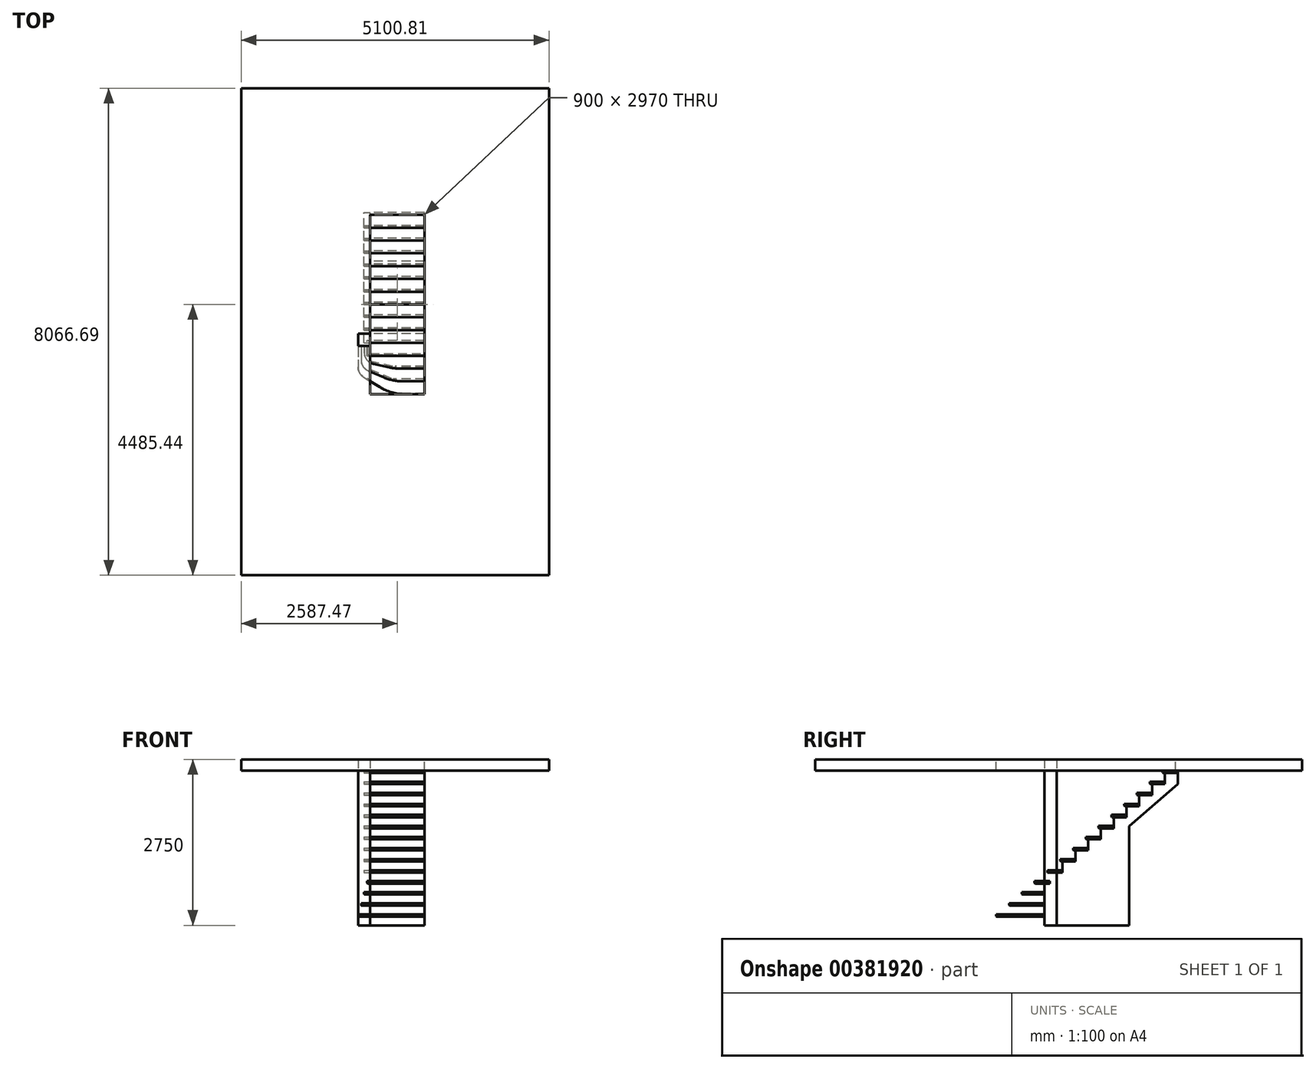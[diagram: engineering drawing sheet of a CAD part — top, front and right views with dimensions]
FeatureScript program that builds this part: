
annotation { "Feature Type Name" : "Feature", "Feature Type Description" : "" }
export const myFeature = defineFeature(function(context is Context, id is Id, definition is map)
    precondition{}
    {
        {
            var Q0;
            Q0=qCreatedBy(makeId("Top.planeOp"),FACE);
            var sketch = newSketch(context, id + "F0", { "sketchPlane" : qUnion([Q0])});
            skLineSegment(sketch, "E0.bottom", {"start": v(0, 2170) * mm, "end": v(-900, 2170) * mm});
            skLineSegment(sketch, "E0.top", {"start": v(0, -800) * mm, "end": v(-900, -800) * mm});
            skLineSegment(sketch, "E0.left", {"start": v(0, 2170) * mm, "end": v(0, -800) * mm});
            skLineSegment(sketch, "E0.right", {"start": v(-900, 2170) * mm, "end": v(-900, -800) * mm});
            skSolve(sketch);
        }
        {
            var Q0;
            Q0=qCreatedBy(makeId("Top.planeOp"),FACE);
            cPlane(context, id + "F1", {"entities" : qUnion([Q0]), "cplaneType" : CPlaneType.OFFSET, "offset" : 2750 * mm, "width" : 150 * mm, "height" : 150 * mm});
        }
        {
            var Q0;
            Q0=qCreatedBy(id+"F1.planeOp",FACE);
            var sketch = newSketch(context, id + "F2", { "sketchPlane" : qUnion([Q0])});
            skLineSegment(sketch, "E1.0", {"start": v(0, 2170) * mm, "end": v(-900, 2170) * mm});
            skLineSegment(sketch, "E1.1", {"start": v(-900, 2170) * mm, "end": v(-900, -800) * mm});
            skLineSegment(sketch, "E1.2", {"start": v(0, -800) * mm, "end": v(-900, -800) * mm});
            skLineSegment(sketch, "E1.3", {"start": v(0, 2170) * mm, "end": v(0, -800) * mm});
            skLineSegment(sketch, "E2.bottom", {"start": v(-3037.47, 4266.25) * mm, "end": v(2063.34, 4266.25) * mm});
            skLineSegment(sketch, "E2.top", {"start": v(-3037.47, -3800.44) * mm, "end": v(2063.34, -3800.44) * mm});
            skLineSegment(sketch, "E2.left", {"start": v(-3037.47, 4266.25) * mm, "end": v(-3037.47, -3800.44) * mm});
            skLineSegment(sketch, "E2.right", {"start": v(2063.34, 4266.25) * mm, "end": v(2063.34, -3800.44) * mm});
            skSolve(sketch);
        }
        {
            var Q0;
            Q0=qCreatedBy(makeId("Top.planeOp"),FACE);
            var sketch = newSketch(context, id + "F3", { "sketchPlane" : qUnion([Q0])});
            skPoint(sketch, "E3.0", {"position": v(0, 0) * mm});
            skLineSegment(sketch, "E4.0", {"start": v(-900, 2170) * mm, "end": v(-900, -800) * mm});
            skLineSegment(sketch, "E5.bottom", {"start": v(-900, 0) * mm, "end": v(-1100, 0) * mm});
            skLineSegment(sketch, "E5.top", {"start": v(-900, 200) * mm, "end": v(-1100, 200) * mm});
            skLineSegment(sketch, "E5.left", {"start": v(-900, 0) * mm, "end": v(-900, 200) * mm});
            skLineSegment(sketch, "E5.right", {"start": v(-1100, 0) * mm, "end": v(-1100, 200) * mm});
            skSolve(sketch);
        }
        {
            var Q0;
            Q0=makeQuery(id+"F3.imprint","IMPRINT",FACE,{"disambiguationData":[TD([[makeQuery(id+"F3.imprint","IMPRINT",EDGE,{"derivedFrom":sQuery(id+"F3.wireOp",EDGE,"E5.bottom")}),-1.0]])]});
            var Q1;
            Q1=qCreatedBy(id+"F1.planeOp",FACE);
            extrude(context, id + "F4", {"entities" : qUnion([Q0]), "endBound" : BoundingType.UP_TO_SURFACE, "endBoundEntityFace" : qUnion([Q1]), "depth" : 25 * mm});
        }
        {
            var Q0;
            Q0=qCreatedBy(makeId("Right.planeOp"),FACE);
            var Q1;
            Q1=sQuery(id+"F0.wireOp",VERTEX,"E0.right.end");
            cPlane(context, id + "F5", {"entities" : qUnion([Q0, Q1]), "cplaneType" : CPlaneType.PLANE_POINT, "offset" : 25 * mm, "width" : 150 * mm, "height" : 150 * mm});
        }
        {
            var Q0;
            Q0=qCreatedBy(id+"F5.planeOp",FACE);
            var sketch = newSketch(context, id + "F6", { "sketchPlane" : qUnion([Q0])});
            skLineSegment(sketch, "E6", {"start": v(-800, 0) * mm, "end": v(-800, 183) * mm});
            skLineSegment(sketch, "E7", {"start": v(-800, 183) * mm, "end": v(-588, 183) * mm});
            skLineSegment(sketch, "E8", {"start": v(-588, 183) * mm, "end": v(-588, 366) * mm});
            skLineSegment(sketch, "E9", {"start": v(-588, 366) * mm, "end": v(-376, 366) * mm});
            skLineSegment(sketch, "E10", {"start": v(-376, 366) * mm, "end": v(-376, 549) * mm});
            skLineSegment(sketch, "E11", {"start": v(-376, 549) * mm, "end": v(-164, 549) * mm});
            skLineSegment(sketch, "E12", {"start": v(-164, 549) * mm, "end": v(-164, 732) * mm});
            skLineSegment(sketch, "E13", {"start": v(-164, 732) * mm, "end": v(48, 732) * mm});
            skLineSegment(sketch, "E14", {"start": v(48, 732) * mm, "end": v(48, 915) * mm});
            skLineSegment(sketch, "E15", {"start": v(48, 915) * mm, "end": v(260, 915) * mm});
            skLineSegment(sketch, "E16", {"start": v(260, 915) * mm, "end": v(260, 1098) * mm});
            skLineSegment(sketch, "E17", {"start": v(260, 1098) * mm, "end": v(472, 1098) * mm});
            skLineSegment(sketch, "E18", {"start": v(472, 1098) * mm, "end": v(472, 1281) * mm});
            skLineSegment(sketch, "E19", {"start": v(472, 1281) * mm, "end": v(684, 1281) * mm});
            skLineSegment(sketch, "E20", {"start": v(684, 1281) * mm, "end": v(684, 1464) * mm});
            skLineSegment(sketch, "E21", {"start": v(684, 1464) * mm, "end": v(896, 1464) * mm});
            skLineSegment(sketch, "E22", {"start": v(896, 1464) * mm, "end": v(896, 1647) * mm});
            skLineSegment(sketch, "E23", {"start": v(896, 1647) * mm, "end": v(1108, 1647) * mm});
            skPoint(sketch, "E24.0", {"position": v(2170, 2750) * mm});
            skLineSegment(sketch, "E25", {"start": v(1108, 1647) * mm, "end": v(1108, 1830) * mm});
            skLineSegment(sketch, "E26", {"start": v(1108, 1830) * mm, "end": v(1320, 1830) * mm});
            skLineSegment(sketch, "E27", {"start": v(1320, 1830) * mm, "end": v(1320, 2013) * mm});
            skLineSegment(sketch, "E28", {"start": v(1320, 2013) * mm, "end": v(1532, 2013) * mm});
            skLineSegment(sketch, "E29", {"start": v(1532, 2013) * mm, "end": v(1532, 2196) * mm});
            skLineSegment(sketch, "E30", {"start": v(1532, 2196) * mm, "end": v(1744, 2196) * mm});
            skLineSegment(sketch, "E31", {"start": v(1744, 2196) * mm, "end": v(1744, 2379) * mm});
            skLineSegment(sketch, "E32", {"start": v(1744, 2379) * mm, "end": v(1956, 2379) * mm});
            skLineSegment(sketch, "E33", {"start": v(1956, 2379) * mm, "end": v(1956, 2562) * mm});
            skLineSegment(sketch, "E34", {"start": v(1956, 2562) * mm, "end": v(2168, 2562) * mm});
            skLineSegment(sketch, "E35", {"start": v(2168, 2562) * mm, "end": v(2168, 2745) * mm});
            skLineSegment(sketch, "E36", {"start": v(2168, 2745) * mm, "end": v(2380, 2745) * mm});
            skSolve(sketch);
        }
        {
            var Q0;
            Q0=qCreatedBy(id+"F5.planeOp",FACE);
            var sketch = newSketch(context, id + "F7", { "sketchPlane" : qUnion([Q0])});
            skLineSegment(sketch, "E37.0", {"start": v(2168, 2745) * mm, "end": v(2380, 2745) * mm});
            skLineSegment(sketch, "E37.1", {"start": v(1956, 2562) * mm, "end": v(2168, 2562) * mm});
            skLineSegment(sketch, "E37.2", {"start": v(1744, 2379) * mm, "end": v(1956, 2379) * mm});
            skLineSegment(sketch, "E37.3", {"start": v(1532, 2196) * mm, "end": v(1744, 2196) * mm});
            skLineSegment(sketch, "E37.4", {"start": v(1320, 2013) * mm, "end": v(1532, 2013) * mm});
            skLineSegment(sketch, "E37.5", {"start": v(1108, 1830) * mm, "end": v(1320, 1830) * mm});
            skLineSegment(sketch, "E37.6", {"start": v(896, 1647) * mm, "end": v(1108, 1647) * mm});
            skLineSegment(sketch, "E37.7", {"start": v(684, 1464) * mm, "end": v(896, 1464) * mm});
            skLineSegment(sketch, "E37.8", {"start": v(472, 1281) * mm, "end": v(684, 1281) * mm});
            skLineSegment(sketch, "E37.9", {"start": v(260, 1098) * mm, "end": v(472, 1098) * mm});
            skLineSegment(sketch, "E37.10", {"start": v(48, 915) * mm, "end": v(260, 915) * mm});
            skLineSegment(sketch, "E38.bottom", {"start": v(1956, 2562) * mm, "end": v(2206, 2562) * mm});
            skLineSegment(sketch, "E38.top", {"start": v(1956, 2522) * mm, "end": v(2206, 2522) * mm});
            skLineSegment(sketch, "E38.left", {"start": v(1956, 2562) * mm, "end": v(1956, 2522) * mm});
            skLineSegment(sketch, "E38.right", {"start": v(2206, 2562) * mm, "end": v(2206, 2522) * mm});
            skLineSegment(sketch, "E39.bottom", {"start": v(1744, 2379) * mm, "end": v(1994, 2379) * mm});
            skLineSegment(sketch, "E39.top", {"start": v(1744, 2339) * mm, "end": v(1994, 2339) * mm});
            skLineSegment(sketch, "E39.left", {"start": v(1744, 2379) * mm, "end": v(1744, 2339) * mm});
            skLineSegment(sketch, "E39.right", {"start": v(1994, 2379) * mm, "end": v(1994, 2339) * mm});
            skLineSegment(sketch, "E40.bottom", {"start": v(1532, 2196) * mm, "end": v(1782, 2196) * mm});
            skLineSegment(sketch, "E40.top", {"start": v(1532, 2156) * mm, "end": v(1782, 2156) * mm});
            skLineSegment(sketch, "E40.left", {"start": v(1532, 2196) * mm, "end": v(1532, 2156) * mm});
            skLineSegment(sketch, "E40.right", {"start": v(1782, 2196) * mm, "end": v(1782, 2156) * mm});
            skLineSegment(sketch, "E41.bottom", {"start": v(1320, 2013) * mm, "end": v(1570, 2013) * mm});
            skLineSegment(sketch, "E41.top", {"start": v(1320, 1973) * mm, "end": v(1570, 1973) * mm});
            skLineSegment(sketch, "E41.left", {"start": v(1320, 2013) * mm, "end": v(1320, 1973) * mm});
            skLineSegment(sketch, "E41.right", {"start": v(1570, 2013) * mm, "end": v(1570, 1973) * mm});
            skLineSegment(sketch, "E42.bottom", {"start": v(1108, 1830) * mm, "end": v(1358, 1830) * mm});
            skLineSegment(sketch, "E42.top", {"start": v(1108, 1790) * mm, "end": v(1358, 1790) * mm});
            skLineSegment(sketch, "E42.left", {"start": v(1108, 1830) * mm, "end": v(1108, 1790) * mm});
            skLineSegment(sketch, "E42.right", {"start": v(1358, 1830) * mm, "end": v(1358, 1790) * mm});
            skLineSegment(sketch, "E43.bottom", {"start": v(896, 1647) * mm, "end": v(1146, 1647) * mm});
            skLineSegment(sketch, "E43.top", {"start": v(896, 1607) * mm, "end": v(1146, 1607) * mm});
            skLineSegment(sketch, "E43.left", {"start": v(896, 1647) * mm, "end": v(896, 1607) * mm});
            skLineSegment(sketch, "E43.right", {"start": v(1146, 1647) * mm, "end": v(1146, 1607) * mm});
            skLineSegment(sketch, "E44.bottom", {"start": v(684, 1464) * mm, "end": v(934, 1464) * mm});
            skLineSegment(sketch, "E44.top", {"start": v(684, 1424) * mm, "end": v(934, 1424) * mm});
            skLineSegment(sketch, "E44.left", {"start": v(684, 1464) * mm, "end": v(684, 1424) * mm});
            skLineSegment(sketch, "E44.right", {"start": v(934, 1464) * mm, "end": v(934, 1424) * mm});
            skLineSegment(sketch, "E45.bottom", {"start": v(472, 1281) * mm, "end": v(722, 1281) * mm});
            skLineSegment(sketch, "E45.top", {"start": v(472, 1241) * mm, "end": v(722, 1241) * mm});
            skLineSegment(sketch, "E45.left", {"start": v(472, 1281) * mm, "end": v(472, 1241) * mm});
            skLineSegment(sketch, "E45.right", {"start": v(722, 1281) * mm, "end": v(722, 1241) * mm});
            skLineSegment(sketch, "E46.bottom", {"start": v(260, 1098) * mm, "end": v(510, 1098) * mm});
            skLineSegment(sketch, "E46.top", {"start": v(260, 1058) * mm, "end": v(510, 1058) * mm});
            skLineSegment(sketch, "E46.left", {"start": v(260, 1098) * mm, "end": v(260, 1058) * mm});
            skLineSegment(sketch, "E46.right", {"start": v(510, 1098) * mm, "end": v(510, 1058) * mm});
            skLineSegment(sketch, "E47.bottom", {"start": v(48, 915) * mm, "end": v(298, 915) * mm});
            skLineSegment(sketch, "E47.top", {"start": v(48, 875) * mm, "end": v(298, 875) * mm});
            skLineSegment(sketch, "E47.left", {"start": v(48, 915) * mm, "end": v(48, 875) * mm});
            skLineSegment(sketch, "E47.right", {"start": v(298, 915) * mm, "end": v(298, 875) * mm});
            skLineSegment(sketch, "E48.0", {"start": v(-164, 732) * mm, "end": v(48, 732) * mm});
            skLineSegment(sketch, "E49.bottom", {"start": v(-164, 732) * mm, "end": v(86, 732) * mm});
            skLineSegment(sketch, "E49.top", {"start": v(-164, 692) * mm, "end": v(86, 692) * mm});
            skLineSegment(sketch, "E49.left", {"start": v(-164, 732) * mm, "end": v(-164, 692) * mm});
            skLineSegment(sketch, "E49.right", {"start": v(86, 732) * mm, "end": v(86, 692) * mm});
            skSolve(sketch);
        }
        {
            var Q0;
            Q0=makeQuery(id+"F7.imprint","IMPRINT",FACE,{"disambiguationData":[TD([[makeQuery(id+"F7.imprint","IMPRINT",EDGE,{"derivedFrom":sQuery(id+"F7.wireOp",EDGE,"E38.top")}),1.0]])]});
            var Q1;
            Q1=makeQuery(id+"F7.imprint","IMPRINT",FACE,{"disambiguationData":[TD([[makeQuery(id+"F7.imprint","IMPRINT",EDGE,{"derivedFrom":sQuery(id+"F7.wireOp",EDGE,"E39.top")}),1.0]])]});
            var Q2;
            Q2=makeQuery(id+"F7.imprint","IMPRINT",FACE,{"disambiguationData":[TD([[makeQuery(id+"F7.imprint","IMPRINT",EDGE,{"derivedFrom":sQuery(id+"F7.wireOp",EDGE,"E40.top")}),1.0]])]});
            var Q3;
            Q3=makeQuery(id+"F7.imprint","IMPRINT",FACE,{"disambiguationData":[TD([[makeQuery(id+"F7.imprint","IMPRINT",EDGE,{"derivedFrom":sQuery(id+"F7.wireOp",EDGE,"E41.top")}),1.0]])]});
            var Q4;
            Q4=makeQuery(id+"F7.imprint","IMPRINT",FACE,{"disambiguationData":[TD([[makeQuery(id+"F7.imprint","IMPRINT",EDGE,{"derivedFrom":sQuery(id+"F7.wireOp",EDGE,"E42.top")}),1.0]])]});
            var Q5;
            Q5=makeQuery(id+"F7.imprint","IMPRINT",FACE,{"disambiguationData":[TD([[makeQuery(id+"F7.imprint","IMPRINT",EDGE,{"derivedFrom":sQuery(id+"F7.wireOp",EDGE,"E43.top")}),1.0]])]});
            var Q6;
            Q6=makeQuery(id+"F7.imprint","IMPRINT",FACE,{"disambiguationData":[TD([[makeQuery(id+"F7.imprint","IMPRINT",EDGE,{"derivedFrom":sQuery(id+"F7.wireOp",EDGE,"E44.top")}),1.0]])]});
            var Q7;
            Q7=makeQuery(id+"F7.imprint","IMPRINT",FACE,{"disambiguationData":[TD([[makeQuery(id+"F7.imprint","IMPRINT",EDGE,{"derivedFrom":sQuery(id+"F7.wireOp",EDGE,"E45.top")}),1.0]])]});
            var Q8;
            Q8=makeQuery(id+"F7.imprint","IMPRINT",FACE,{"disambiguationData":[TD([[makeQuery(id+"F7.imprint","IMPRINT",EDGE,{"derivedFrom":sQuery(id+"F7.wireOp",EDGE,"E46.top")}),1.0]])]});
            var Q9;
            Q9=makeQuery(id+"F7.imprint","IMPRINT",FACE,{"disambiguationData":[TD([[makeQuery(id+"F7.imprint","IMPRINT",EDGE,{"derivedFrom":sQuery(id+"F7.wireOp",EDGE,"E47.top")}),1.0]])]});
            var Q10;
            Q10=makeQuery(id+"F7.imprint","IMPRINT",FACE,{"disambiguationData":[TD([[makeQuery(id+"F7.imprint","IMPRINT",EDGE,{"derivedFrom":sQuery(id+"F7.wireOp",EDGE,"E49.top")}),1.0]])]});
            var Q11;
            Q11=qCreatedBy(makeId("Right.planeOp"),FACE);
            extrude(context, id + "F8", {"entities" : qUnion([Q0, Q1, Q2, Q3, Q4, Q5, Q6, Q7, Q8, Q9, Q10]), "endBound" : BoundingType.UP_TO_SURFACE, "endBoundEntityFace" : qUnion([Q11]), "depth" : 25 * mm});
        }
        {
            var Q0;
            Q0=makeQuery(id+"F8.opExtrude","CAP_FACE",FACE,{"disambiguationData":[OSD([sQuery(id+"F7.wireOp",EDGE,"E38.bottom"),sQuery(id+"F7.wireOp",EDGE,"E38.top"),sQuery(id+"F7.wireOp",EDGE,"E38.left"),sQuery(id+"F7.wireOp",EDGE,"E38.right")])],"isStart":true});
            var Q1;
            Q1=makeQuery(id+"F8.opExtrude","CAP_FACE",FACE,{"disambiguationData":[OSD([sQuery(id+"F7.wireOp",EDGE,"E39.bottom"),sQuery(id+"F7.wireOp",EDGE,"E39.top"),sQuery(id+"F7.wireOp",EDGE,"E39.left"),sQuery(id+"F7.wireOp",EDGE,"E39.right")])],"isStart":true});
            var Q2;
            Q2=makeQuery(id+"F8.opExtrude","CAP_FACE",FACE,{"disambiguationData":[OSD([sQuery(id+"F7.wireOp",EDGE,"E40.bottom"),sQuery(id+"F7.wireOp",EDGE,"E40.top"),sQuery(id+"F7.wireOp",EDGE,"E40.left"),sQuery(id+"F7.wireOp",EDGE,"E40.right")])],"isStart":true});
            var Q3;
            Q3=makeQuery(id+"F8.opExtrude","CAP_FACE",FACE,{"disambiguationData":[OSD([sQuery(id+"F7.wireOp",EDGE,"E41.bottom"),sQuery(id+"F7.wireOp",EDGE,"E41.top"),sQuery(id+"F7.wireOp",EDGE,"E41.left"),sQuery(id+"F7.wireOp",EDGE,"E41.right")])],"isStart":true});
            var Q4;
            Q4=makeQuery(id+"F8.opExtrude","CAP_FACE",FACE,{"disambiguationData":[OSD([sQuery(id+"F7.wireOp",EDGE,"E42.bottom"),sQuery(id+"F7.wireOp",EDGE,"E42.top"),sQuery(id+"F7.wireOp",EDGE,"E42.left"),sQuery(id+"F7.wireOp",EDGE,"E42.right")])],"isStart":true});
            var Q5;
            Q5=makeQuery(id+"F8.opExtrude","CAP_FACE",FACE,{"disambiguationData":[OSD([sQuery(id+"F7.wireOp",EDGE,"E43.bottom"),sQuery(id+"F7.wireOp",EDGE,"E43.top"),sQuery(id+"F7.wireOp",EDGE,"E43.left"),sQuery(id+"F7.wireOp",EDGE,"E43.right")])],"isStart":true});
            var Q6;
            Q6=makeQuery(id+"F8.opExtrude","CAP_FACE",FACE,{"disambiguationData":[OSD([sQuery(id+"F7.wireOp",EDGE,"E44.bottom"),sQuery(id+"F7.wireOp",EDGE,"E44.top"),sQuery(id+"F7.wireOp",EDGE,"E44.left"),sQuery(id+"F7.wireOp",EDGE,"E44.right")])],"isStart":true});
            var Q7;
            Q7=makeQuery(id+"F8.opExtrude","CAP_FACE",FACE,{"disambiguationData":[OSD([sQuery(id+"F7.wireOp",EDGE,"E45.bottom"),sQuery(id+"F7.wireOp",EDGE,"E45.top"),sQuery(id+"F7.wireOp",EDGE,"E45.left"),sQuery(id+"F7.wireOp",EDGE,"E45.right")])],"isStart":true});
            var Q8;
            Q8=makeQuery(id+"F8.opExtrude","CAP_FACE",FACE,{"disambiguationData":[OSD([sQuery(id+"F7.wireOp",EDGE,"E46.bottom"),sQuery(id+"F7.wireOp",EDGE,"E46.top"),sQuery(id+"F7.wireOp",EDGE,"E46.left"),sQuery(id+"F7.wireOp",EDGE,"E46.right")])],"isStart":true});
            var Q9;
            Q9=makeQuery(id+"F8.opExtrude","CAP_FACE",FACE,{"disambiguationData":[OSD([sQuery(id+"F7.wireOp",EDGE,"E47.bottom"),sQuery(id+"F7.wireOp",EDGE,"E47.top"),sQuery(id+"F7.wireOp",EDGE,"E47.left"),sQuery(id+"F7.wireOp",EDGE,"E47.right")])],"isStart":true});
            extrude(context, id + "F9", {"entities" : qUnion([Q0, Q1, Q2, Q3, Q4, Q5, Q6, Q7, Q8, Q9]), "depth" : 100 * mm});
        }
        {
            var Q0;
            Q0=qCreatedBy(id+"F5.planeOp",FACE);
            var sketch = newSketch(context, id + "F10", { "sketchPlane" : qUnion([Q0])});
            skLineSegment(sketch, "E50.0", {"start": v(298, 915) * mm, "end": v(298, 875) * mm});
            skLineSegment(sketch, "E50.1", {"start": v(510, 1098) * mm, "end": v(510, 1058) * mm});
            skLineSegment(sketch, "E50.2", {"start": v(722, 1281) * mm, "end": v(722, 1241) * mm});
            skLineSegment(sketch, "E50.3", {"start": v(934, 1464) * mm, "end": v(934, 1424) * mm});
            skLineSegment(sketch, "E50.4", {"start": v(1146, 1647) * mm, "end": v(1146, 1607) * mm});
            skLineSegment(sketch, "E50.5", {"start": v(1358, 1830) * mm, "end": v(1358, 1790) * mm});
            skLineSegment(sketch, "E50.6", {"start": v(1570, 2013) * mm, "end": v(1570, 1973) * mm});
            skLineSegment(sketch, "E50.7", {"start": v(1782, 2196) * mm, "end": v(1782, 2156) * mm});
            skLineSegment(sketch, "E50.8", {"start": v(1994, 2379) * mm, "end": v(1994, 2339) * mm});
            skLineSegment(sketch, "E50.9", {"start": v(2206, 2562) * mm, "end": v(2206, 2522) * mm});
            skLineSegment(sketch, "E51", {"start": v(298, 915) * mm, "end": v(298, 1058) * mm});
            skLineSegment(sketch, "E52", {"start": v(298, 1058) * mm, "end": v(510, 1058) * mm});
            skLineSegment(sketch, "E53", {"start": v(510, 1098) * mm, "end": v(510, 1241) * mm});
            skLineSegment(sketch, "E54", {"start": v(510, 1241) * mm, "end": v(722, 1241) * mm});
            skLineSegment(sketch, "E55", {"start": v(722, 1281) * mm, "end": v(722, 1424) * mm});
            skLineSegment(sketch, "E56", {"start": v(722, 1424) * mm, "end": v(934, 1424) * mm});
            skLineSegment(sketch, "E57", {"start": v(934, 1464) * mm, "end": v(934, 1607) * mm});
            skLineSegment(sketch, "E58", {"start": v(934, 1607) * mm, "end": v(1146, 1607) * mm});
            skLineSegment(sketch, "E59", {"start": v(1146, 1647) * mm, "end": v(1146, 1790) * mm});
            skLineSegment(sketch, "E60", {"start": v(1146, 1790) * mm, "end": v(1358, 1790) * mm});
            skLineSegment(sketch, "E61", {"start": v(1358, 1830) * mm, "end": v(1358, 1973) * mm});
            skLineSegment(sketch, "E62", {"start": v(1358, 1973) * mm, "end": v(1570, 1973) * mm});
            skLineSegment(sketch, "E63", {"start": v(1570, 2013) * mm, "end": v(1570, 2156) * mm});
            skLineSegment(sketch, "E64", {"start": v(1570, 2156) * mm, "end": v(1782, 2156) * mm});
            skLineSegment(sketch, "E65", {"start": v(1782, 2196) * mm, "end": v(1782, 2339) * mm});
            skLineSegment(sketch, "E66", {"start": v(1782, 2339) * mm, "end": v(1994, 2339) * mm});
            skLineSegment(sketch, "E67", {"start": v(1994, 2379) * mm, "end": v(1994, 2522) * mm});
            skLineSegment(sketch, "E68", {"start": v(1994, 2522) * mm, "end": v(2206, 2522) * mm});
            skPoint(sketch, "E69.0", {"position": v(200, 875) * mm});
            skLineSegment(sketch, "E70", {"start": v(298, 875) * mm, "end": v(200, 875) * mm});
            skLineSegment(sketch, "E71", {"start": v(200, 0) * mm, "end": v(1400, 0) * mm});
            skLineSegment(sketch, "E72", {"start": v(1400, 0) * mm, "end": v(1400, 1973) * mm});
            skLineSegment(sketch, "E73", {"start": v(200, 875) * mm, "end": v(200, 0) * mm});
            skLineSegment(sketch, "E74", {"start": v(2206, 2522) * mm, "end": v(2206, 2339) * mm});
            skLineSegment(sketch, "E75", {"start": v(1146, 1607) * mm, "end": v(1146, 1424) * mm});
            skLineSegment(sketch, "E76", {"start": v(1146, 1424) * mm, "end": v(2206, 2339) * mm});
            skSolve(sketch);
        }
        {
            var Q0;
            Q0=makeQuery(id+"F10.imprint","IMPRINT",FACE,{"disambiguationData":[TD([[makeQuery(id+"F10.imprint","IMPRINT",EDGE,{"derivedFrom":sQuery(id+"F10.wireOp",EDGE,"E50.0")}),1.0]])]});
            var Q1;
            Q1=makeQuery(id+"F10.imprint","IMPRINT",FACE,{"disambiguationData":[TD([[makeQuery(id+"F10.imprint","IMPRINT",EDGE,{"derivedFrom":sQuery(id+"F10.wireOp",EDGE,"E50.4")}),1.0]])]});
            var Q2;
            {var subQ0=sQuery(id+"F10.wireOp",EDGE,"E50.6");Q2=makeQuery(id+"F10.imprint","IMPRINT",FACE,{"disambiguationData":[TD([[makeQuery(id+"F10.imprint","IMPRINT",EDGE,{"derivedFrom":subQ0}),1.0]])]});}
            var Q3;
            Q3=qCreatedBy(makeId("Right.planeOp"),FACE);
            extrude(context, id + "F11", {"entities" : qUnion([Q0, Q1, Q2]), "endBound" : BoundingType.UP_TO_SURFACE, "endBoundEntityFace" : qUnion([Q3]), "depth" : 25 * mm});
        }
        {
            var Q0;
            Q0=makeQuery(id+"F8.opExtrude","CAP_FACE",FACE,{"disambiguationData":[OSD([sQuery(id+"F7.wireOp",EDGE,"E49.bottom"),sQuery(id+"F7.wireOp",EDGE,"E49.top"),sQuery(id+"F7.wireOp",EDGE,"E49.left"),sQuery(id+"F7.wireOp",EDGE,"E49.right")])],"isStart":true});
            extrude(context, id + "F12", {"entities" : qUnion([Q0]), "depth" : 50 * mm});
        }
        {
            var Q0;
            Q0=qCreatedBy(makeId("Top.planeOp"),FACE);
            var Q1;
            Q1=sQuery(id+"F6.wireOp",VERTEX,"E11.start");
            cPlane(context, id + "F13", {"entities" : qUnion([Q0, Q1]), "cplaneType" : CPlaneType.PLANE_POINT, "offset" : 25 * mm, "width" : 150 * mm, "height" : 150 * mm});
        }
        {
            var Q0;
            Q0=qCreatedBy(makeId("Top.planeOp"),FACE);
            var Q1;
            Q1=sQuery(id+"F6.wireOp",VERTEX,"E9.start");
            cPlane(context, id + "F14", {"entities" : qUnion([Q0, Q1]), "cplaneType" : CPlaneType.PLANE_POINT, "offset" : 25 * mm, "width" : 150 * mm, "height" : 150 * mm});
        }
        {
            var Q0;
            Q0=qCreatedBy(makeId("Top.planeOp"),FACE);
            var Q1;
            Q1=sQuery(id+"F6.wireOp",VERTEX,"E7.start");
            cPlane(context, id + "F15", {"entities" : qUnion([Q0, Q1]), "cplaneType" : CPlaneType.PLANE_POINT, "offset" : 25 * mm, "width" : 150 * mm, "height" : 150 * mm});
        }
        {
            var Q0;
            Q0=qCreatedBy(id+"F13.planeOp",FACE);
            var sketch = newSketch(context, id + "F16", { "sketchPlane" : qUnion([Q0])});
            skPoint(sketch, "E77.0", {"position": v(-900, -376) * mm});
            skLineSegment(sketch, "E78.bottom", {"start": v(-500, -376) * mm, "end": v(0, -376) * mm});
            skLineSegment(sketch, "E78.top", {"start": v(-900, -126) * mm, "end": v(0, -126) * mm});
            skLineSegment(sketch, "E78.right", {"start": v(0, -376) * mm, "end": v(0, -126) * mm});
            skLineSegment(sketch, "E79", {"start": v(-1000, -126) * mm, "end": v(-1000, -266) * mm});
            skLineSegment(sketch, "E80", {"start": v(-1000, -266) * mm, "end": v(-500, -376) * mm});
            skLineSegment(sketch, "E81.0", {"start": v(-900, 0) * mm, "end": v(-1000, 0) * mm});
            skLineSegment(sketch, "E82", {"start": v(-900, -126) * mm, "end": v(-900, 0) * mm});
            skLineSegment(sketch, "E83", {"start": v(-1000, -126) * mm, "end": v(-1000, 0) * mm});
            skPoint(sketch, "E84.orphan", {"position": v(-1100, 0) * mm});
            skSolve(sketch);
        }
        {
            var Q0;
            Q0=makeQuery(id+"F16.imprint","IMPRINT",FACE,{"disambiguationData":[TD([[makeQuery(id+"F16.imprint","IMPRINT",EDGE,{"derivedFrom":sQuery(id+"F16.wireOp",EDGE,"E78.bottom")}),1.0]])]});
            extrude(context, id + "F17", {"entities" : qUnion([Q0]), "oppositeDirection" : true, "depth" : 40 * mm});
        }
        {
            var Q0;
            Q0=qCreatedBy(id+"F14.planeOp",FACE);
            var sketch = newSketch(context, id + "F18", { "sketchPlane" : qUnion([Q0])});
            skPoint(sketch, "E85.0", {"position": v(-900, -588) * mm});
            skLineSegment(sketch, "E86", {"start": v(-525, -588) * mm, "end": v(0, -588) * mm});
            skLineSegment(sketch, "E87", {"start": v(0, -588) * mm, "end": v(0, -338) * mm});
            skPoint(sketch, "E88", {"position": v(-525, -588) * mm});
            skPoint(sketch, "E89", {"position": v(-1000, -226) * mm});
            skLineSegment(sketch, "E90", {"start": v(0, -338) * mm, "end": v(-490.9, -338) * mm});
            skLineSegment(sketch, "E91", {"start": v(-900, -248) * mm, "end": v(-490.9, -338) * mm});
            skPoint(sketch, "E92.orphan", {"position": v(-1000, -266) * mm});
            skLineSegment(sketch, "E93", {"start": v(-1050, -226) * mm, "end": v(-1050, -366) * mm});
            skLineSegment(sketch, "E94", {"start": v(-1050, -366) * mm, "end": v(-525, -588) * mm});
            skLineSegment(sketch, "E95.0", {"start": v(-900, 0) * mm, "end": v(-1050, 0) * mm});
            skLineSegment(sketch, "E96", {"start": v(-900, 0) * mm, "end": v(-900, -248) * mm});
            skLineSegment(sketch, "E97", {"start": v(-1050, -226) * mm, "end": v(-1050, 0) * mm});
            skPoint(sketch, "E98.orphan", {"position": v(-1100, 0) * mm});
            skSolve(sketch);
        }
        {
            var Q0;
            Q0=makeQuery(id+"F18.imprint","IMPRINT",FACE,{"disambiguationData":[TD([[makeQuery(id+"F18.imprint","IMPRINT",EDGE,{"derivedFrom":sQuery(id+"F18.wireOp",EDGE,"E86")}),1.0]])]});
            extrude(context, id + "F19", {"entities" : qUnion([Q0]), "oppositeDirection" : true, "depth" : 40 * mm});
        }
        {
            var Q0;
            Q0=qCreatedBy(id+"F15.planeOp",FACE);
            var sketch = newSketch(context, id + "F20", { "sketchPlane" : qUnion([Q0])});
            skPoint(sketch, "E99.0", {"position": v(-900, -800) * mm});
            skLineSegment(sketch, "E100", {"start": v(-550, -800) * mm, "end": v(0, -800) * mm});
            skLineSegment(sketch, "E101", {"start": v(0, -800) * mm, "end": v(0, -550) * mm});
            skLineSegment(sketch, "E102", {"start": v(0, -550) * mm, "end": v(-520.27, -550) * mm});
            skPoint(sketch, "E103", {"position": v(-550, -800) * mm});
            skPoint(sketch, "E104", {"position": v(-1050, -326) * mm});
            skLineSegment(sketch, "E105", {"start": v(-900, -389.43) * mm, "end": v(-520.27, -550) * mm});
            skLineSegment(sketch, "E106.0", {"start": v(-900, 0) * mm, "end": v(-1100, 0) * mm});
            skLineSegment(sketch, "E107", {"start": v(-900, 0) * mm, "end": v(-900, -389.43) * mm});
            skLineSegment(sketch, "E108", {"start": v(-900, -389.43) * mm, "end": v(-900, 0) * mm});
            skLineSegment(sketch, "E109", {"start": v(-1100, -326) * mm, "end": v(-1100, -466) * mm});
            skPoint(sketch, "E110.orphan", {"position": v(-1050, -366) * mm});
            skPoint(sketch, "E111.0.end.orphan", {"position": v(-1050, 0) * mm});
            skLineSegment(sketch, "E112", {"start": v(-1100, 0) * mm, "end": v(-1100, -326) * mm});
            skLineSegment(sketch, "E113", {"start": v(-1100, -466) * mm, "end": v(-550, -800) * mm});
            skSolve(sketch);
        }
        {
            var Q0;
            Q0=makeQuery(id+"F20.imprint","IMPRINT",FACE,{"disambiguationData":[TD([[makeQuery(id+"F20.imprint","IMPRINT",EDGE,{"derivedFrom":sQuery(id+"F20.wireOp",EDGE,"E100")}),1.0]])]});
            extrude(context, id + "F21", {"entities" : qUnion([Q0]), "oppositeDirection" : true, "depth" : 40 * mm});
        }
        {
            var Q0;
            Q0=makeQuery(id+"F21.opExtrude","CAP_FACE",FACE,{"disambiguationData":[OSD([sQuery(id+"F20.wireOp",EDGE,"E100"),sQuery(id+"F20.wireOp",EDGE,"E101"),sQuery(id+"F20.wireOp",EDGE,"E102"),sQuery(id+"F20.wireOp",EDGE,"E105"),sQuery(id+"F20.wireOp",EDGE,"E106.0"),sQuery(id+"F20.wireOp",EDGE,"E108"),sQuery(id+"F20.wireOp",EDGE,"E109"),sQuery(id+"F20.wireOp",EDGE,"E112"),sQuery(id+"F20.wireOp",EDGE,"E113")])],"isStart":false});
            var sketch = newSketch(context, id + "F22", { "sketchPlane" : qUnion([Q0])});
            skLineSegment(sketch, "E114.0", {"start": v(-538.8, 760) * mm, "end": v(0, 760) * mm});
            skLineSegment(sketch, "E114.1", {"start": v(-1060, 443.5) * mm, "end": v(-538.8, 760) * mm});
            skLineSegment(sketch, "E114.2", {"start": v(-1060, 0) * mm, "end": v(-1060, 443.5) * mm});
            skSolve(sketch);
        }
        {
            var Q0;
            Q0=sQuery(id+"F22.wireOp",EDGE,"E114.2");
            var Q1;
            Q1=sQuery(id+"F22.wireOp",EDGE,"E114.1");
            var Q2;
            Q2=sQuery(id+"F22.wireOp",EDGE,"E114.0");
            var Q3;
            Q3=makeQuery(id+"F4.opExtrude","CAP_FACE",FACE,{"disambiguationData":[OSD([sQuery(id+"F3.wireOp",EDGE,"E5.bottom"),sQuery(id+"F3.wireOp",EDGE,"E5.top"),sQuery(id+"F3.wireOp",EDGE,"E5.left"),sQuery(id+"F3.wireOp",EDGE,"E5.right")])],"isStart":true});
            extrude(context, id + "F23", {"bodyType" : ToolBodyType.SURFACE, "surfaceEntities" : qUnion([Q0, Q1, Q2]), "endBound" : BoundingType.UP_TO_SURFACE, "endBoundEntityFace" : qUnion([Q3]), "depth" : 25 * mm});
        }
        {
            var Q0;
            Q0=makeQuery(id+"F19.opExtrude","CAP_FACE",FACE,{"disambiguationData":[OSD([sQuery(id+"F18.wireOp",EDGE,"E86"),sQuery(id+"F18.wireOp",EDGE,"E87"),sQuery(id+"F18.wireOp",EDGE,"E90"),sQuery(id+"F18.wireOp",EDGE,"E91"),sQuery(id+"F18.wireOp",EDGE,"E93"),sQuery(id+"F18.wireOp",EDGE,"E94"),sQuery(id+"F18.wireOp",EDGE,"E95.0"),sQuery(id+"F18.wireOp",EDGE,"E96"),sQuery(id+"F18.wireOp",EDGE,"E97")])],"isStart":false});
            var sketch = newSketch(context, id + "F24", { "sketchPlane" : qUnion([Q0])});
            skLineSegment(sketch, "E115.0", {"start": v(-1010, 339.49) * mm, "end": v(-1010, 0) * mm});
            skLineSegment(sketch, "E115.1", {"start": v(-1010, 339.49) * mm, "end": v(-516.9, 548) * mm});
            skLineSegment(sketch, "E115.2", {"start": v(-516.9, 548) * mm, "end": v(0, 548) * mm});
            skSolve(sketch);
        }
        {
            var Q0;
            Q0=sQuery(id+"F24.wireOp",EDGE,"E115.0");
            var Q1;
            Q1=sQuery(id+"F24.wireOp",EDGE,"E115.1");
            var Q2;
            Q2=sQuery(id+"F24.wireOp",EDGE,"E115.2");
            var Q3;
            Q3=makeQuery(id+"F21.opExtrude","CAP_FACE",FACE,{"disambiguationData":[OSD([sQuery(id+"F20.wireOp",EDGE,"E100"),sQuery(id+"F20.wireOp",EDGE,"E101"),sQuery(id+"F20.wireOp",EDGE,"E102"),sQuery(id+"F20.wireOp",EDGE,"E105"),sQuery(id+"F20.wireOp",EDGE,"E106.0"),sQuery(id+"F20.wireOp",EDGE,"E108"),sQuery(id+"F20.wireOp",EDGE,"E109"),sQuery(id+"F20.wireOp",EDGE,"E112"),sQuery(id+"F20.wireOp",EDGE,"E113")])],"isStart":true});
            extrude(context, id + "F25", {"bodyType" : ToolBodyType.SURFACE, "surfaceEntities" : qUnion([Q0, Q1, Q2]), "endBound" : BoundingType.UP_TO_SURFACE, "endBoundEntityFace" : qUnion([Q3]), "depth" : 25 * mm});
        }
        {
            var Q0;
            Q0=makeQuery(id+"F17.opExtrude","CAP_FACE",FACE,{"disambiguationData":[OSD([sQuery(id+"F16.wireOp",EDGE,"E78.bottom"),sQuery(id+"F16.wireOp",EDGE,"E78.top"),sQuery(id+"F16.wireOp",EDGE,"E78.right"),sQuery(id+"F16.wireOp",EDGE,"E79"),sQuery(id+"F16.wireOp",EDGE,"E80"),sQuery(id+"F16.wireOp",EDGE,"E81.0"),sQuery(id+"F16.wireOp",EDGE,"E82"),sQuery(id+"F16.wireOp",EDGE,"E83")])],"isStart":false});
            var sketch = newSketch(context, id + "F26", { "sketchPlane" : qUnion([Q0])});
            skLineSegment(sketch, "E116.0", {"start": v(-960, 233.84) * mm, "end": v(-960, 0) * mm});
            skLineSegment(sketch, "E116.1", {"start": v(-960, 233.84) * mm, "end": v(-495.65, 336) * mm});
            skLineSegment(sketch, "E116.2", {"start": v(-495.65, 336) * mm, "end": v(0, 336) * mm});
            skSolve(sketch);
        }
        {
            var Q0;
            Q0=sQuery(id+"F26.wireOp",EDGE,"E116.0");
            var Q1;
            Q1=sQuery(id+"F26.wireOp",EDGE,"E116.1");
            var Q2;
            Q2=sQuery(id+"F26.wireOp",EDGE,"E116.2");
            var Q3;
            Q3=makeQuery(id+"F19.opExtrude","CAP_FACE",FACE,{"disambiguationData":[OSD([sQuery(id+"F18.wireOp",EDGE,"E86"),sQuery(id+"F18.wireOp",EDGE,"E87"),sQuery(id+"F18.wireOp",EDGE,"E90"),sQuery(id+"F18.wireOp",EDGE,"E91"),sQuery(id+"F18.wireOp",EDGE,"E93"),sQuery(id+"F18.wireOp",EDGE,"E94"),sQuery(id+"F18.wireOp",EDGE,"E95.0"),sQuery(id+"F18.wireOp",EDGE,"E96"),sQuery(id+"F18.wireOp",EDGE,"E97")])],"isStart":true});
            extrude(context, id + "F27", {"bodyType" : ToolBodyType.SURFACE, "surfaceEntities" : qUnion([Q0, Q1, Q2]), "endBound" : BoundingType.UP_TO_SURFACE, "endBoundEntityFace" : qUnion([Q3]), "depth" : 25 * mm});
        }
        {
            var Q0;
            Q0=makeQuery(id+"F8.opExtrude","SWEPT_FACE",FACE,{"disambiguationData":[OSD([sQuery(id+"F7.wireOp",EDGE,"E49.top")])]});
            var sketch = newSketch(context, id + "F28", { "sketchPlane" : qUnion([Q0])});
            skLineSegment(sketch, "E117.0", {"start": v(-910, 124) * mm, "end": v(-910, -86) * mm});
            skLineSegment(sketch, "E117.1", {"start": v(-910, 124) * mm, "end": v(-900, 124) * mm});
            skLineSegment(sketch, "E117.2", {"start": v(0, 124) * mm, "end": v(-900, 124) * mm});
            skSolve(sketch);
        }
        {
            var Q0;
            Q0=sQuery(id+"F28.wireOp",EDGE,"E117.0");
            var Q1;
            Q1=sQuery(id+"F28.wireOp",EDGE,"E117.1");
            var Q2;
            Q2=sQuery(id+"F28.wireOp",EDGE,"E117.2");
            var Q3;
            Q3=makeQuery(id+"F17.opExtrude","CAP_FACE",FACE,{"disambiguationData":[OSD([sQuery(id+"F16.wireOp",EDGE,"E78.bottom"),sQuery(id+"F16.wireOp",EDGE,"E78.top"),sQuery(id+"F16.wireOp",EDGE,"E78.right"),sQuery(id+"F16.wireOp",EDGE,"E79"),sQuery(id+"F16.wireOp",EDGE,"E80"),sQuery(id+"F16.wireOp",EDGE,"E81.0"),sQuery(id+"F16.wireOp",EDGE,"E82"),sQuery(id+"F16.wireOp",EDGE,"E83")])],"isStart":true});
            extrude(context, id + "F29", {"bodyType" : ToolBodyType.SURFACE, "surfaceEntities" : qUnion([Q0, Q1, Q2]), "endBound" : BoundingType.UP_TO_SURFACE, "endBoundEntityFace" : qUnion([Q3]), "depth" : 25 * mm});
        }
        {
            var Q0;
            Q0=makeQuery(id+"F8.opExtrude","SWEPT_FACE",FACE,{"disambiguationData":[OSD([sQuery(id+"F7.wireOp",EDGE,"E49.bottom")])]});
            var sketch = newSketch(context, id + "F30", { "sketchPlane" : qUnion([Q0])});
            skLineSegment(sketch, "E118.0", {"start": v(0, 86) * mm, "end": v(-900, 86) * mm});
            skSolve(sketch);
        }
        {
            var Q0;
            Q0=sQuery(id+"F30.wireOp",EDGE,"E118.0");
            var Q1;
            Q1=makeQuery(id+"F8.opExtrude","SWEPT_FACE",FACE,{"disambiguationData":[OSD([sQuery(id+"F7.wireOp",EDGE,"E47.top")])]});
            extrude(context, id + "F31", {"bodyType" : ToolBodyType.SURFACE, "surfaceEntities" : qUnion([Q0]), "endBound" : BoundingType.UP_TO_SURFACE, "endBoundEntityFace" : qUnion([Q1]), "depth" : 25 * mm});
        }
        {
            var Q0;
            Q0=makeQuery(id+"F9.opExtrude","SWEPT_EDGE",EDGE,{"disambiguationData":[OSD([sQuery(id+"F7.wireOp",EDGE,"E38.top"),sQuery(id+"F7.wireOp",EDGE,"E38.left")])]});
            var Q1;
            Q1=makeQuery(id+"F8.opExtrude","SWEPT_EDGE",EDGE,{"disambiguationData":[OSD([sQuery(id+"F7.wireOp",EDGE,"E38.top"),sQuery(id+"F7.wireOp",EDGE,"E38.left")])]});
            var Q2;
            Q2=makeQuery(id+"F9.opExtrude","SWEPT_EDGE",EDGE,{"disambiguationData":[OSD([sQuery(id+"F7.wireOp",EDGE,"E39.top"),sQuery(id+"F7.wireOp",EDGE,"E39.left")])]});
            var Q3;
            Q3=makeQuery(id+"F8.opExtrude","SWEPT_EDGE",EDGE,{"disambiguationData":[OSD([sQuery(id+"F7.wireOp",EDGE,"E39.top"),sQuery(id+"F7.wireOp",EDGE,"E39.left")])]});
            var Q4;
            Q4=makeQuery(id+"F9.opExtrude","SWEPT_EDGE",EDGE,{"disambiguationData":[OSD([sQuery(id+"F7.wireOp",EDGE,"E40.top"),sQuery(id+"F7.wireOp",EDGE,"E40.left")])]});
            var Q5;
            Q5=makeQuery(id+"F8.opExtrude","SWEPT_EDGE",EDGE,{"disambiguationData":[OSD([sQuery(id+"F7.wireOp",EDGE,"E40.top"),sQuery(id+"F7.wireOp",EDGE,"E40.left")])]});
            var Q6;
            Q6=makeQuery(id+"F9.opExtrude","SWEPT_EDGE",EDGE,{"disambiguationData":[OSD([sQuery(id+"F7.wireOp",EDGE,"E41.top"),sQuery(id+"F7.wireOp",EDGE,"E41.left")])]});
            var Q7;
            Q7=makeQuery(id+"F8.opExtrude","SWEPT_EDGE",EDGE,{"disambiguationData":[OSD([sQuery(id+"F7.wireOp",EDGE,"E41.top"),sQuery(id+"F7.wireOp",EDGE,"E41.left")])]});
            var Q8;
            Q8=makeQuery(id+"F9.opExtrude","SWEPT_EDGE",EDGE,{"disambiguationData":[OSD([sQuery(id+"F7.wireOp",EDGE,"E42.top"),sQuery(id+"F7.wireOp",EDGE,"E42.left")])]});
            var Q9;
            Q9=makeQuery(id+"F8.opExtrude","SWEPT_EDGE",EDGE,{"disambiguationData":[OSD([sQuery(id+"F7.wireOp",EDGE,"E42.top"),sQuery(id+"F7.wireOp",EDGE,"E42.left")])]});
            var Q10;
            Q10=makeQuery(id+"F9.opExtrude","SWEPT_EDGE",EDGE,{"disambiguationData":[OSD([sQuery(id+"F7.wireOp",EDGE,"E43.top"),sQuery(id+"F7.wireOp",EDGE,"E43.left")])]});
            var Q11;
            Q11=makeQuery(id+"F8.opExtrude","SWEPT_EDGE",EDGE,{"disambiguationData":[OSD([sQuery(id+"F7.wireOp",EDGE,"E43.top"),sQuery(id+"F7.wireOp",EDGE,"E43.left")])]});
            var Q12;
            Q12=makeQuery(id+"F9.opExtrude","SWEPT_EDGE",EDGE,{"disambiguationData":[OSD([sQuery(id+"F7.wireOp",EDGE,"E44.top"),sQuery(id+"F7.wireOp",EDGE,"E44.left")])]});
            var Q13;
            Q13=makeQuery(id+"F8.opExtrude","SWEPT_EDGE",EDGE,{"disambiguationData":[OSD([sQuery(id+"F7.wireOp",EDGE,"E44.top"),sQuery(id+"F7.wireOp",EDGE,"E44.left")])]});
            var Q14;
            Q14=makeQuery(id+"F9.opExtrude","SWEPT_EDGE",EDGE,{"disambiguationData":[OSD([sQuery(id+"F7.wireOp",EDGE,"E45.top"),sQuery(id+"F7.wireOp",EDGE,"E45.left")])]});
            var Q15;
            Q15=makeQuery(id+"F8.opExtrude","SWEPT_EDGE",EDGE,{"disambiguationData":[OSD([sQuery(id+"F7.wireOp",EDGE,"E45.top"),sQuery(id+"F7.wireOp",EDGE,"E45.left")])]});
            var Q16;
            Q16=makeQuery(id+"F9.opExtrude","SWEPT_EDGE",EDGE,{"disambiguationData":[OSD([sQuery(id+"F7.wireOp",EDGE,"E46.top"),sQuery(id+"F7.wireOp",EDGE,"E46.left")])]});
            var Q17;
            Q17=makeQuery(id+"F8.opExtrude","SWEPT_EDGE",EDGE,{"disambiguationData":[OSD([sQuery(id+"F7.wireOp",EDGE,"E46.top"),sQuery(id+"F7.wireOp",EDGE,"E46.left")])]});
            var Q18;
            Q18=makeQuery(id+"F8.opExtrude","SWEPT_EDGE",EDGE,{"disambiguationData":[OSD([sQuery(id+"F7.wireOp",EDGE,"E47.top"),sQuery(id+"F7.wireOp",EDGE,"E47.left")])]});
            var Q19;
            {var subQ0=sQuery(id+"F7.wireOp",EDGE,"E49.left");var subQ1=sQuery(id+"F7.wireOp",EDGE,"E49.top");Q19=makeQuery(id+"F12.boolean.opBoolean","MERGE",EDGE,{"derivedFrom":[makeQuery(id+"F8.opExtrude","SWEPT_EDGE",EDGE,{"disambiguationData":[OSD([subQ1,subQ0])]}),makeQuery(id+"F12.opExtrude","SWEPT_EDGE",EDGE,{"disambiguationData":[OSD([subQ1,subQ0])]})]});}
            var Q20;
            Q20=makeQuery(id+"F12.opExtrude","CAP_EDGE",EDGE,{"disambiguationData":[OSD([sQuery(id+"F7.wireOp",EDGE,"E49.top")])],"isStart":false});
            var Q21;
            Q21=makeQuery(id+"F17.opExtrude","CAP_EDGE",EDGE,{"disambiguationData":[OSD([sQuery(id+"F16.wireOp",EDGE,"E79"),sQuery(id+"F16.wireOp",EDGE,"E83")])],"isStart":false});
            var Q22;
            Q22=makeQuery(id+"F17.opExtrude","CAP_EDGE",EDGE,{"disambiguationData":[OSD([sQuery(id+"F16.wireOp",EDGE,"E80")])],"isStart":false});
            var Q23;
            Q23=makeQuery(id+"F17.opExtrude","CAP_EDGE",EDGE,{"disambiguationData":[OSD([sQuery(id+"F16.wireOp",EDGE,"E78.bottom")])],"isStart":false});
            var Q24;
            Q24=makeQuery(id+"F19.opExtrude","CAP_EDGE",EDGE,{"disambiguationData":[OSD([sQuery(id+"F18.wireOp",EDGE,"E93"),sQuery(id+"F18.wireOp",EDGE,"E97")])],"isStart":false});
            var Q25;
            Q25=makeQuery(id+"F19.opExtrude","CAP_EDGE",EDGE,{"disambiguationData":[OSD([sQuery(id+"F18.wireOp",EDGE,"E94")])],"isStart":false});
            var Q26;
            Q26=makeQuery(id+"F19.opExtrude","CAP_EDGE",EDGE,{"disambiguationData":[OSD([sQuery(id+"F18.wireOp",EDGE,"E86")])],"isStart":false});
            var Q27;
            Q27=makeQuery(id+"F21.opExtrude","CAP_EDGE",EDGE,{"disambiguationData":[OSD([sQuery(id+"F20.wireOp",EDGE,"E109"),sQuery(id+"F20.wireOp",EDGE,"E112")])],"isStart":false});
            var Q28;
            Q28=makeQuery(id+"F21.opExtrude","CAP_EDGE",EDGE,{"disambiguationData":[OSD([sQuery(id+"F20.wireOp",EDGE,"E113")])],"isStart":false});
            var Q29;
            Q29=makeQuery(id+"F21.opExtrude","CAP_EDGE",EDGE,{"disambiguationData":[OSD([sQuery(id+"F20.wireOp",EDGE,"E100")])],"isStart":false});
            chamfer(context, id + "F32", {"entities" : qUnion([Q0, Q1, Q2, Q3, Q4, Q5, Q6, Q7, Q8, Q9, Q10, Q11, Q12, Q13, Q14, Q15, Q16, Q17, Q18, Q19, Q20, Q21, Q22, Q23, Q24, Q25, Q26, Q27, Q28, Q29]), "width" : 10 * mm, "tangentPropagation" : true});
        }
        {
            var Q0;
            Q0=makeQuery(id+"F36.opExtrude","CAP_FACE",FACE,{"disambiguationData":[OSD([sQuery(id+"F2.wireOp",EDGE,"E1.0"),sQuery(id+"F2.wireOp",EDGE,"E1.1"),sQuery(id+"F2.wireOp",EDGE,"E1.2"),sQuery(id+"F2.wireOp",EDGE,"E1.3"),sQuery(id+"F2.wireOp",EDGE,"E2.bottom"),sQuery(id+"F2.wireOp",EDGE,"E2.top"),sQuery(id+"F2.wireOp",EDGE,"E2.left"),sQuery(id+"F2.wireOp",EDGE,"E2.right")])],"isStart":false});
            var sketch = newSketch(context, id + "F33", { "sketchPlane" : qUnion([Q0])});
            skPoint(sketch, "E119.0", {"position": v(-950, -1956) * mm});
            skCircle(sketch, "E120", {"center": v(-950, -1903.5) * mm, "radius": 5 * mm});
            skCircle(sketch, "E121", {"center": v(-950, -1796.5) * mm, "radius": 5 * mm});
            skCircle(sketch, "E122", {"center": v(-950, -1691.5) * mm, "radius": 5 * mm});
            skCircle(sketch, "E123", {"center": v(-950, -1584.5) * mm, "radius": 5 * mm});
            skCircle(sketch, "E124", {"center": v(-950, -1479.5) * mm, "radius": 5 * mm});
            skCircle(sketch, "E125", {"center": v(-950, -1372.5) * mm, "radius": 5 * mm});
            skCircle(sketch, "E126", {"center": v(-950, -1267.5) * mm, "radius": 5 * mm});
            skCircle(sketch, "E127", {"center": v(-950, -1160.5) * mm, "radius": 5 * mm});
            skCircle(sketch, "E128", {"center": v(-950, -1055.5) * mm, "radius": 5 * mm});
            skCircle(sketch, "E129", {"center": v(-950, -948.5) * mm, "radius": 5 * mm});
            skCircle(sketch, "E130", {"center": v(-950, -843.5) * mm, "radius": 5 * mm});
            skCircle(sketch, "E131", {"center": v(-950, -736.5) * mm, "radius": 5 * mm});
            skCircle(sketch, "E132", {"center": v(-950, -631.5) * mm, "radius": 5 * mm});
            skCircle(sketch, "E133", {"center": v(-950, -524.5) * mm, "radius": 5 * mm});
            skCircle(sketch, "E134", {"center": v(-950, -419.5) * mm, "radius": 5 * mm});
            skCircle(sketch, "E135", {"center": v(-950, -312.5) * mm, "radius": 5 * mm});
            skSolve(sketch);
        }
        {
            var Q0;
            Q0=makeQuery(id+"F17.opExtrude","SWEPT_EDGE",EDGE,{"disambiguationData":[OSD([sQuery(id+"F16.wireOp",EDGE,"E78.bottom"),sQuery(id+"F16.wireOp",EDGE,"E80")])]});
            var Q1;
            Q1=makeQuery(id+"F19.opExtrude","SWEPT_EDGE",EDGE,{"disambiguationData":[OSD([sQuery(id+"F18.wireOp",EDGE,"E86"),sQuery(id+"F18.wireOp",EDGE,"E94")])]});
            var Q2;
            Q2=makeQuery(id+"F21.opExtrude","SWEPT_EDGE",EDGE,{"disambiguationData":[OSD([sQuery(id+"F20.wireOp",EDGE,"E100"),sQuery(id+"F20.wireOp",EDGE,"E113")])]});
            fillet(context, id + "F34", {"entities" : qUnion([Q0, Q1, Q2]), "radius" : 800 * mm, "tangentPropagation" : true, "allowEdgeOverflow" : false});
        }
        {
            var Q0;
            Q0=makeQuery(id+"F19.opExtrude","SWEPT_EDGE",EDGE,{"disambiguationData":[OSD([sQuery(id+"F18.wireOp",EDGE,"E93"),sQuery(id+"F18.wireOp",EDGE,"E94")])]});
            var Q1;
            Q1=makeQuery(id+"F17.opExtrude","SWEPT_EDGE",EDGE,{"disambiguationData":[OSD([sQuery(id+"F16.wireOp",EDGE,"E79"),sQuery(id+"F16.wireOp",EDGE,"E80")])]});
            var Q2;
            Q2=makeQuery(id+"F21.opExtrude","SWEPT_EDGE",EDGE,{"disambiguationData":[OSD([sQuery(id+"F20.wireOp",EDGE,"E109"),sQuery(id+"F20.wireOp",EDGE,"E113")])]});
            fillet(context, id + "F35", {"entities" : qUnion([Q0, Q1, Q2]), "radius" : 200 * mm, "tangentPropagation" : true, "allowEdgeOverflow" : false});
        }
        {
            var Q0;
            Q0=makeQuery(id+"F2.imprint","IMPRINT",FACE,{"disambiguationData":[TD([[makeQuery(id+"F2.imprint","IMPRINT",EDGE,{"derivedFrom":sQuery(id+"F2.wireOp",EDGE,"E1.0")}),-1.0]])]});
            extrude(context, id + "F36", {"entities" : qUnion([Q0]), "oppositeDirection" : true, "depth" : 188 * mm});
        }
    });
